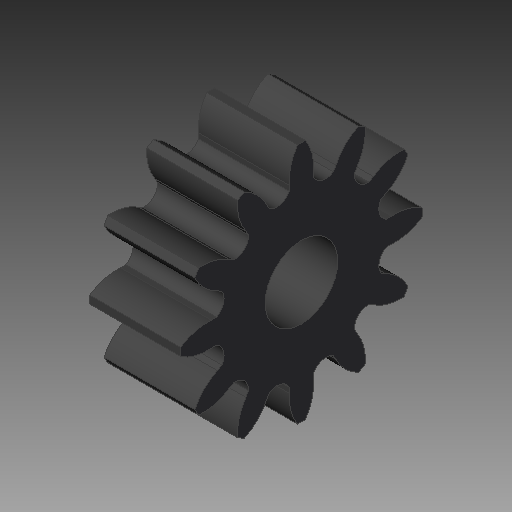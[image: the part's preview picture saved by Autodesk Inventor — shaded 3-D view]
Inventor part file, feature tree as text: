
AUTODESK INVENTOR PART (.ipt)
format: ipt  version: 2018 (Build 220112000, 112)  size: 254,976 bytes
history: native  units: in
note: dims shown in document units (in); Inventor stores cm internally (conversion verified against a paired STEP export)
features: other x3, sketch x3
ambient origin geometry x8: Origin, YZ Plane, XZ Plane, XY Plane, X Axis, Y Axis, Z Axis, Center Point
bodies: Solid1 (feature_tree)
feature tree (6):
  other  "Pinion final.ipt"
  other  "Solid1::Pinion final.ipt"
  other  "TaggingFeature1"
  sketch  "Sketch6"  dims[d0=0.3937in]
  sketch  "Sketch7"
  sketch  "Sketch8"
